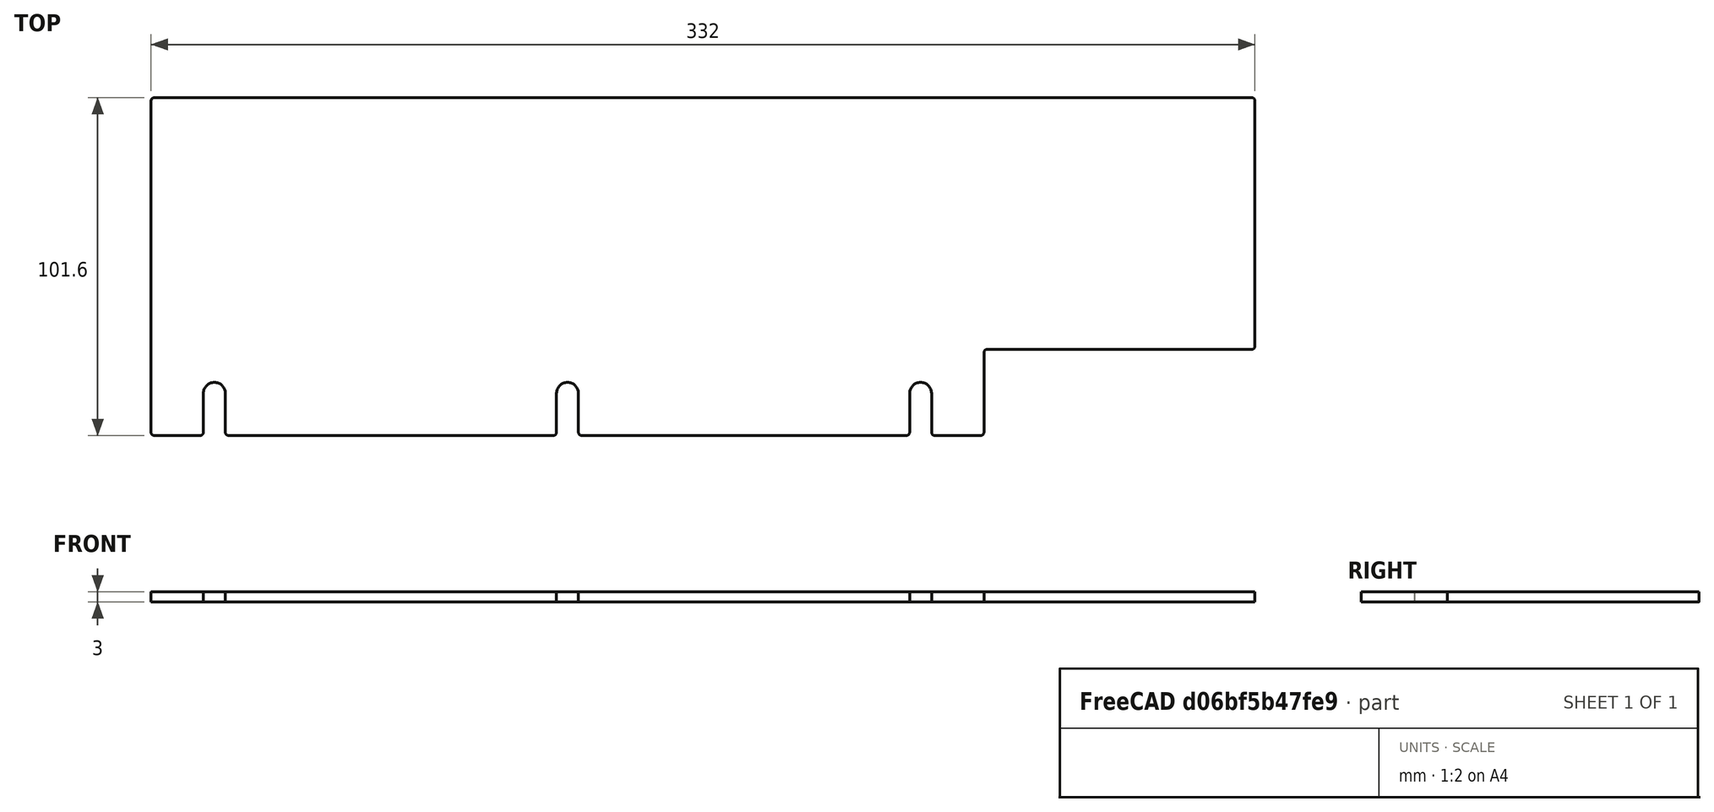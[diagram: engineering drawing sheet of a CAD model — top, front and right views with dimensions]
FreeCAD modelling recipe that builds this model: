
FCSTD DOCUMENT  (FreeCAD 0.21R33675 (Git))
Label: right_wall_front
License: All rights reserved
LicenseURL: http://en.wikipedia.org/wiki/All_rights_reserved
objects: Spreadsheet::Sheet×1, Sketcher::SketchObject×1, PartDesign::Pad×1, PartDesign::Body×1
note: 4 computed .brp shape members not serialized (recipe doc carries the construction recipe); baked Part::Feature solids carry a one-line shape summary decoded from their .brp

FEATURE [Spreadsheet::Sheet] Spreadsheet
  cells = A2='Parameters; A3='ServoOffsetFromCenter; B3(ServoOffsetFromCenter)==-3 in; A4='BeamLength; B4(BeamLength)==18 in; A5='BracketLength; B5(BracketLength)==108.6 mm; A6='DistanceLeftBracketEdgeToDoor; B6(DistanceLeftBracketEdgeToDoor)==82.4999 mm; A7='DistanceRightBracketEdgeToDoor; B7(DistanceRightBracketEdgeToDoor)==23.1001 mm; A8='DoorMargin; B8(DoorMargin)==1 mm; A9='LengthMargin; B9(LengthMargin)==0 mm; A10='LengthLeftBracketEdgeToDoorGap; B10(LengthLeftBracketEdgeToDoorGap)==DistanceLeftBracketEdgeToDoor - DoorMargin; A11='LengthRightBracketEdgeToDoorGap; B11(LengthRightBracketEdgeToDoorGap)==DistanceRightBracketEdgeToDoor - DoorMargin; A12='LengthDoorGap; B12(LengthDoorGap)==BracketLength - LengthLeftBracketEdgeToDoorGap - LengthRightBracketEdgeToDoorGap; A13='BeamLengthMinusBracketLength; B13(BeamLengthMinusBracketLength)==BeamLength - BracketLength; A14='DistanceFrontToDoor; B14(DistanceFrontToDoor)==0.5 * BeamLengthMinusBracketLength + LengthLeftBracketEdgeToDoorGap - ServoOffsetFromCenter; A15='DistanceFrontToBracket; B15(DistanceFrontToBracket)==0.5 * BeamLengthMinusBracketLength - ServoOffsetFromCenter; A16='LengthFrontToDoor; B16(LengthFrontToDoor)==DistanceFrontToDoor - LengthMargin; A17='LengthFrontToBracket; B17(LengthFrontToBracket)==DistanceFrontToBracket - LengthMargin; A18='Height; B18(Height)==4 in; A19='Thickness; B19(Thickness)==3 mm; A20='CutoutMargin; B20(CutoutMargin)==0.5 mm; A21='CutoutHeight; B21(CutoutHeight)==1 in + CutoutMargin; A22='FilletRadius; B22(FilletRadius)==1 mm; A23='MountHoleDiameter; B23(MountHoleDiameter)==0.26 in; A24='MountHoleDistanceFromBottom; B24(MountHoleDistanceFromBottom)==0.5 in; A25='MountHoleSideMargin; B25(MountHoleSideMargin)==0.75 in
FEATURE [Sketcher::SketchObject] Sketch
  FullyConstrained = true
  MapMode = 5
  Support = -> [XY_Plane]
  expr: Constraints[14] = Spreadsheet.FilletRadius
  expr: Constraints[20] = Spreadsheet.Height
  expr: Constraints[43] = Spreadsheet.MountHoleDistanceFromBottom
  expr: Constraints[44] = Spreadsheet.MountHoleDiameter
  expr: Constraints[64] = Spreadsheet.MountHoleSideMargin
  expr: Constraints[7] = Spreadsheet.LengthFrontToDoor
  expr: Constraints[8] = Spreadsheet.LengthFrontToBracket
  expr: Constraints[9] = Spreadsheet.CutoutHeight
  sketch-geometry (50):
    g0: LineSegment StartX=0 StartY=100.6 StartZ=0 EndX=0 EndY=1 EndZ=0
    g1: LineSegment StartX=1 StartY=0 StartZ=0 EndX=249.5 EndY=0 EndZ=0
    g2: LineSegment StartX=250.5 StartY=1 StartZ=0 EndX=250.5 EndY=24.9 EndZ=0
    g3: LineSegment StartX=251.5 StartY=25.9 StartZ=0 EndX=331 EndY=25.9 EndZ=0
    g4: LineSegment StartX=332 StartY=26.9 StartZ=0 EndX=332 EndY=100.6 EndZ=0
    g5: LineSegment StartX=331 StartY=101.6 StartZ=0 EndX=1 EndY=101.6 EndZ=0
    g6: ArcOfCircle CenterX=1 CenterY=100.6 CenterZ=0 NormalX=0 NormalY=0 NormalZ=1 AngleXU=0 Radius=1 StartAngle=1.5708 EndAngle=3.14159
    g7: GeomPoint X=0 Y=101.6 Z=0
    g8: ArcOfCircle CenterX=1 CenterY=1 CenterZ=0 NormalX=0 NormalY=0 NormalZ=1 AngleXU=0 Radius=1 StartAngle=3.14159 EndAngle=4.71239
    g9: GeomPoint X=0 Y=0 Z=0
    g10: ArcOfCircle CenterX=249.5 CenterY=1 CenterZ=0 NormalX=0 NormalY=0 NormalZ=1 AngleXU=0 Radius=1 StartAngle=4.71239 EndAngle=6.28319
    g11: GeomPoint X=250.5 Y=0 Z=0
    g12: ArcOfCircle CenterX=251.5 CenterY=24.9 CenterZ=0 NormalX=0 NormalY=0 NormalZ=1 AngleXU=0 Radius=1 StartAngle=1.5708 EndAngle=3.14159
    g13: GeomPoint X=250.5 Y=25.9 Z=0
    g14: ArcOfCircle CenterX=331 CenterY=26.9 CenterZ=0 NormalX=0 NormalY=0 NormalZ=1 AngleXU=0 Radius=1 StartAngle=4.71239 EndAngle=6.28319
    g15: GeomPoint X=332 Y=25.9 Z=0
    g16: ArcOfCircle CenterX=331 CenterY=100.6 CenterZ=0 NormalX=0 NormalY=0 NormalZ=1 AngleXU=0 Radius=1 StartAngle=-3.6e-15 EndAngle=1.5708
    g17: GeomPoint X=332 Y=101.6 Z=0
    g18: GeomPoint X=125.25 Y=0 Z=0
    g19: LineSegment StartX=125.25 StartY=0 StartZ=0 EndX=125.25 EndY=12.7 EndZ=0
    g20: Circle CenterX=125.25 CenterY=12.7 CenterZ=0 NormalX=0 NormalY=0 NormalZ=1 AngleXU=0 Radius=3.302
    g21: LineSegment StartX=19.05 StartY=0 StartZ=0 EndX=19.05 EndY=12.7 EndZ=0
    g22: LineSegment StartX=231.45 StartY=0 StartZ=0 EndX=231.45 EndY=12.7 EndZ=0
    g23: Circle CenterX=19.05 CenterY=12.7 CenterZ=0 NormalX=0 NormalY=0 NormalZ=1 AngleXU=0 Radius=3.302
    g24: Circle CenterX=231.45 CenterY=12.7 CenterZ=0 NormalX=0 NormalY=0 NormalZ=1 AngleXU=0 Radius=3.302
    g25: LineSegment StartX=19.05 StartY=12.7 StartZ=0 EndX=0 EndY=12.7 EndZ=0
    g26: LineSegment StartX=231.45 StartY=12.7 StartZ=0 EndX=250.5 EndY=12.7 EndZ=0
    g27: ArcOfCircle CenterX=19.05 CenterY=12.7 CenterZ=0 NormalX=0 NormalY=0 NormalZ=1 AngleXU=0 Radius=3.302 StartAngle=0 EndAngle=3.14159
    g28: LineSegment StartX=19.05 StartY=12.7 StartZ=0 EndX=22.352 EndY=12.7 EndZ=0
    g29: LineSegment StartX=15.748 StartY=12.7 StartZ=0 EndX=15.748 EndY=1 EndZ=0
    g30: LineSegment StartX=22.352 StartY=12.7 StartZ=0 EndX=22.352 EndY=1 EndZ=0
    g31: ArcOfCircle CenterX=14.748 CenterY=1 CenterZ=0 NormalX=0 NormalY=0 NormalZ=1 AngleXU=0 Radius=1 StartAngle=4.71239 EndAngle=6.28319
    g32: ArcOfCircle CenterX=23.352 CenterY=1 CenterZ=0 NormalX=0 NormalY=0 NormalZ=1 AngleXU=0 Radius=1 StartAngle=3.14159 EndAngle=4.71239
    g33: LineSegment StartX=121.948 StartY=12.7 StartZ=0 EndX=121.948 EndY=1 EndZ=0
    g34: LineSegment StartX=128.552 StartY=12.7 StartZ=0 EndX=128.552 EndY=1 EndZ=0
    g35: ArcOfCircle CenterX=120.948 CenterY=1 CenterZ=0 NormalX=0 NormalY=0 NormalZ=1 AngleXU=0 Radius=1 StartAngle=4.71239 EndAngle=6.28319
    g36: ArcOfCircle CenterX=129.552 CenterY=1 CenterZ=0 NormalX=0 NormalY=0 NormalZ=1 AngleXU=0 Radius=1 StartAngle=3.14159 EndAngle=4.71239
    g37: ArcOfCircle CenterX=125.25 CenterY=12.7 CenterZ=0 NormalX=0 NormalY=0 NormalZ=1 AngleXU=0 Radius=3.302 StartAngle=-3.6e-15 EndAngle=3.14159
    g38: LineSegment StartX=125.25 StartY=12.7 StartZ=0 EndX=121.948 EndY=12.7 EndZ=0
    g39: LineSegment StartX=125.25 StartY=12.7 StartZ=0 EndX=128.552 EndY=12.7 EndZ=0
    g40: LineSegment StartX=228.148 StartY=12.7 StartZ=0 EndX=228.148 EndY=1 EndZ=0
    g41: LineSegment StartX=234.752 StartY=12.7 StartZ=0 EndX=234.752 EndY=1 EndZ=0
    g42: ArcOfCircle CenterX=227.148 CenterY=1 CenterZ=0 NormalX=0 NormalY=0 NormalZ=1 AngleXU=0 Radius=1 StartAngle=4.71239 EndAngle=6.28319
    g43: ArcOfCircle CenterX=235.752 CenterY=1 CenterZ=0 NormalX=0 NormalY=0 NormalZ=1 AngleXU=0 Radius=1 StartAngle=3.14159 EndAngle=4.71239
    g44: ArcOfCircle CenterX=231.45 CenterY=12.7 CenterZ=0 NormalX=0 NormalY=0 NormalZ=1 AngleXU=0 Radius=3.302 StartAngle=3.4e-15 EndAngle=3.14159
    g45: LineSegment StartX=231.45 StartY=12.7 StartZ=0 EndX=228.148 EndY=12.7 EndZ=0
    g46: LineSegment StartX=1 StartY=0 StartZ=0 EndX=14.748 EndY=0 EndZ=0
    g47: LineSegment StartX=23.352 StartY=0 StartZ=0 EndX=120.948 EndY=0 EndZ=0
    g48: LineSegment StartX=129.552 StartY=0 StartZ=0 EndX=227.148 EndY=0 EndZ=0
    g49: LineSegment StartX=235.752 StartY=0 StartZ=0 EndX=249.5 EndY=0 EndZ=0
  constraints (126):
    c: Vertical(g0)
    c: Horizontal(g1)
    c: Vertical(g2)
    c: Horizontal(g3)
    c: Vertical(g4)
    c: Horizontal(g5)
    c: Coincident(g-1,g9)
    c: DistanceX(g7,g17) = 332
    c: DistanceX(g9,g11) = 250.5
    c: DistanceY(g11,g13) = 25.9
    c: PointOnObject(g7,g0)
    c: PointOnObject(g7,g5)
    c: Tangent(g0,g6) = -1.5708
    c: Tangent(g5,g6) = -1.5708
    c: Radius(g6) = 1
    c: PointOnObject(g9,g0)
    c: PointOnObject(g9,g1)
    c: Tangent(g0,g8) = -1.5708
    c: Tangent(g1,g8) = -1.5708
    c: Equal(g8,g6)
    c: DistanceY(g1,g5) = 101.6
    c: PointOnObject(g11,g1)
    c: PointOnObject(g11,g2)
    c: Tangent(g1,g10) = -1.5708
    c: Tangent(g2,g10) = -1.5708
    c: Equal(g10,g8)
    c: PointOnObject(g13,g2)
    c: PointOnObject(g13,g3)
    c: Tangent(g2,g12) = 1.5708
    c: Tangent(g3,g12) = 1.5708
    c: Equal(g12,g10)
    c: PointOnObject(g15,g3)
    c: PointOnObject(g15,g4)
    c: Tangent(g3,g14) = -1.5708
    c: Tangent(g4,g14) = -1.5708
    c: Equal(g14,g12)
    c: PointOnObject(g17,g5)
    c: PointOnObject(g17,g4)
    c: Tangent(g5,g16) = -1.5708
    c: Tangent(g4,g16) = -1.5708
    c: Equal(g16,g14)
    c: Coincident(g19,g18)
    c: Vertical(g19)
    c: DistanceY(g19,g19) = 12.7
    c: Diameter(g20) = 6.604
    c: Coincident(g19,g20)
    c: Symmetric(g1,g1,g18)
    c: Vertical(g21)
    c: Vertical(g22)
    c: PointOnObject(g21,g1)
    c: PointOnObject(g22,g1)
    c: Equal(g21,g19)
    c: Equal(g19,g22)
    c: Equal(g23,g20)
    c: Equal(g20,g24)
    c: Coincident(g23,g21)
    c: Coincident(g24,g22)
    c: Coincident(g25,g23)
    c: PointOnObject(g25,g0)
    c: Horizontal(g25)
    c: Coincident(g26,g24)
    c: PointOnObject(g26,g2)
    c: Horizontal(g26)
    c: Equal(g25,g26)
    c: DistanceX(g25,g25) = 19.05
    c: Coincident(g27,g21)
    c: PointOnObject(g27,g25)
    c: Coincident(g28,g27)
    c: Coincident(g28,g27)
    c: Horizontal(g28)
    c: PointOnObject(g27,g23)
    c: Coincident(g29,g27)
    c: Vertical(g29)
    c: Coincident(g30,g27)
    c: Vertical(g30)
    c: Equal(g29,g30)
    c: Tangent(g31,g29) = 1.5708
    c: Tangent(g31,g1) = -1.5708
    c: Tangent(g32,g30) = -1.5708
    c: Tangent(g32,g1) = -1.5708
    c: Equal(g31,g8)
    c: Coincident(g33,g37)
    c: Vertical(g33)
    c: Coincident(g34,g37)
    c: Vertical(g34)
    c: Equal(g33,g34)
    c: Tangent(g35,g33) = 1.5708
    c: Tangent(g36,g34) = -1.5708
    c: Coincident(g38,g19)
    c: Horizontal(g38)
    c: Coincident(g39,g19)
    c: Horizontal(g39)
    c: PointOnObject(g38,g20)
    c: PointOnObject(g39,g20)
    c: PointOnObject(g33,g38)
    c: PointOnObject(g33,g20)
    c: PointOnObject(g34,g39)
    c: Coincident(g37,g19)
    c: Tangent(g35,g1) = -1.5708
    c: Tangent(g36,g1) = -1.5708
    c: Equal(g36,g10)
    c: Coincident(g40,g44)
    c: Vertical(g40)
    c: Coincident(g41,g44)
    c: Vertical(g41)
    c: Equal(g40,g41)
    c: Tangent(g42,g40) = 1.5708
    c: Tangent(g43,g41) = -1.5708
    c: Horizontal(g45)
    c: PointOnObject(g40,g45)
    c: PointOnObject(g41,g26)
    c: PointOnObject(g40,g24)
    c: PointOnObject(g45,g24)
    c: Coincident(g45,g22)
    c: Coincident(g44,g22)
    c: Tangent(g42,g1) = -1.5708
    c: Tangent(g43,g1) = -1.5708
    c: Equal(g43,g10)
    c: Coincident(g46,g8)
    c: Coincident(g46,g31)
    c: Coincident(g47,g32)
    c: Coincident(g47,g35)
    c: Coincident(g48,g36)
    c: Coincident(g48,g42)
    c: Coincident(g49,g43)
    c: Coincident(g49,g10)
FEATURE [PartDesign::Pad] Pad
  Direction = (0,0,1)
  Length = 3
  Length2 = 10
  Profile = -> Sketch
  ReferenceAxis = -> Sketch [N_Axis]
  Type = 0
  expr: Length = Spreadsheet.Thickness
FEATURE [PartDesign::Body] Body
  Group = -> [Sketch,Pad]
  Origin = -> Origin
  Tip = -> Pad
